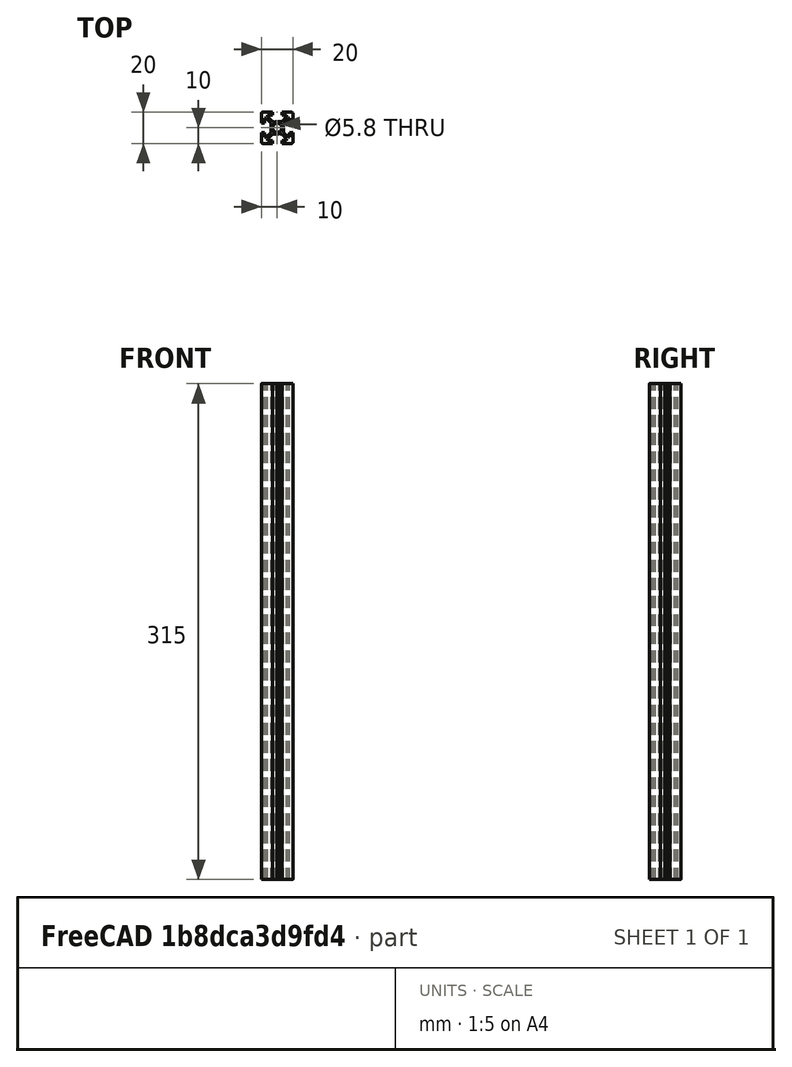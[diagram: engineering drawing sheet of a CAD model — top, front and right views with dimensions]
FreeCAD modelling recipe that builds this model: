
FCSTD DOCUMENT  (FreeCAD 0.17R13519 (Git))
Label: Z_Profile_2020_bed_side
License: All rights reserved
LicenseURL: http://en.wikipedia.org/wiki/All_rights_reserved
objects: Sketcher::SketchObject×1, PartDesign::Pad×1, PartDesign::Body×1
note: 4 computed .brp shape members not serialized (recipe doc carries the construction recipe); baked Part::Feature solids carry a one-line shape summary decoded from their .brp

FEATURE [Sketcher::SketchObject] Sketch001
  MapMode = 4
  sketch-geometry (77):
    g0: LineSegment StartX=-8 StartY=-3 StartZ=0 EndX=-10 EndY=-3 EndZ=0
    g1: LineSegment StartX=-10 StartY=-3 StartZ=0 EndX=-10 EndY=-9 EndZ=0
    g2: ArcOfCircle CenterX=-9 CenterY=-9 CenterZ=0 NormalX=0 NormalY=0 NormalZ=1 AngleXU=0 Radius=1 StartAngle=3.14159 EndAngle=4.71239
    g3: LineSegment StartX=-9 StartY=-10 StartZ=0 EndX=-3 EndY=-10 EndZ=0
    g4: LineSegment StartX=-3 StartY=-10 StartZ=0 EndX=-3 EndY=-8 EndZ=0
    g5: LineSegment StartX=-3 StartY=-8 StartZ=0 EndX=-6 EndY=-8 EndZ=0
    g6: LineSegment StartX=-6 StartY=-8 StartZ=0 EndX=-6 EndY=-7.06066 EndZ=0
    g7: LineSegment StartX=-6 StartY=-7.06066 StartZ=0 EndX=-2.93934 EndY=-4 EndZ=0
    g8: LineSegment StartX=-2.93934 StartY=-4 StartZ=0 EndX=-0.65359 EndY=-4 EndZ=0
    g9: ArcOfCircle CenterX=-0.65359 CenterY=-3.5 CenterZ=0 NormalX=0 NormalY=0 NormalZ=1 AngleXU=0 Radius=0.5 StartAngle=4.71239 EndAngle=5.23599
    g10: LineSegment StartX=-0.40359 StartY=-3.93301 StartZ=0 EndX=0 EndY=-3.7 EndZ=0
    g11: LineSegment StartX=0 StartY=-3.7 StartZ=0 EndX=0.40359 EndY=-3.93301 EndZ=0
    g12: ArcOfCircle CenterX=0.65359 CenterY=-3.5 CenterZ=0 NormalX=0 NormalY=0 NormalZ=1 AngleXU=0 Radius=0.5 StartAngle=4.18879 EndAngle=5.23599
    g13: LineSegment StartX=0.90359 StartY=-3.93301 StartZ=0 EndX=1.21889 EndY=-3.75098 EndZ=0
    g14: LineSegment StartX=1.21889 StartY=-3.75098 StartZ=0 EndX=2.5 EndY=-4 EndZ=0
    g15: LineSegment StartX=2.5 StartY=-4 StartZ=0 EndX=2.93934 EndY=-4 EndZ=0
    g16: LineSegment StartX=2.93934 StartY=-4 StartZ=0 EndX=6 EndY=-7.06066 EndZ=0
    g17: LineSegment StartX=6 StartY=-7.06066 StartZ=0 EndX=6 EndY=-8 EndZ=0
    g18: LineSegment StartX=6 StartY=-8 StartZ=0 EndX=3 EndY=-8 EndZ=0
    g19: LineSegment StartX=3 StartY=-8 StartZ=0 EndX=3 EndY=-10 EndZ=0
    g20: LineSegment StartX=3 StartY=-10 StartZ=0 EndX=9 EndY=-10 EndZ=0
    g21: ArcOfCircle CenterX=9 CenterY=-9 CenterZ=0 NormalX=0 NormalY=0 NormalZ=1 AngleXU=0 Radius=1 StartAngle=4.71239 EndAngle=6.28319
    g22: LineSegment StartX=10 StartY=-9 StartZ=0 EndX=10 EndY=-3 EndZ=0
    g23: LineSegment StartX=10 StartY=-3 StartZ=0 EndX=8 EndY=-3 EndZ=0
    g24: LineSegment StartX=8 StartY=-3 StartZ=0 EndX=8 EndY=-6 EndZ=0
    g25: LineSegment StartX=8 StartY=-6 StartZ=0 EndX=7.06066 EndY=-6 EndZ=0
    g26: LineSegment StartX=7.06066 StartY=-6 StartZ=0 EndX=4 EndY=-2.93934 EndZ=0
    g27: LineSegment StartX=4 StartY=-2.93934 StartZ=0 EndX=4 EndY=-0.65359 EndZ=0
    g28: ArcOfCircle CenterX=3.5 CenterY=-0.65359 CenterZ=0 NormalX=0 NormalY=0 NormalZ=1 AngleXU=0 Radius=0.5 StartAngle=0 EndAngle=0.523599
    g29: LineSegment StartX=3.93301 StartY=-0.40359 StartZ=0 EndX=3.7 EndY=0 EndZ=0
    g30: LineSegment StartX=3.7 StartY=0 StartZ=0 EndX=3.93301 EndY=0.40359 EndZ=0
    g31: ArcOfCircle CenterX=3.5 CenterY=0.65359 CenterZ=0 NormalX=0 NormalY=0 NormalZ=1 AngleXU=0 Radius=0.5 StartAngle=5.75959 EndAngle=6.80678
    g32: LineSegment StartX=3.93301 StartY=0.90359 StartZ=0 EndX=3.75098 EndY=1.21889 EndZ=0
    g33: LineSegment StartX=3.75098 StartY=1.21889 StartZ=0 EndX=4 EndY=2.5 EndZ=0
    g34: LineSegment StartX=4 StartY=2.5 StartZ=0 EndX=4 EndY=2.93934 EndZ=0
    g35: LineSegment StartX=4 StartY=2.93934 StartZ=0 EndX=7.06066 EndY=6 EndZ=0
    g36: LineSegment StartX=7.06066 StartY=6 StartZ=0 EndX=8 EndY=6 EndZ=0
    g37: LineSegment StartX=8 StartY=6 StartZ=0 EndX=8 EndY=3 EndZ=0
    g38: LineSegment StartX=8 StartY=3 StartZ=0 EndX=10 EndY=3 EndZ=0
    g39: LineSegment StartX=10 StartY=3 StartZ=0 EndX=10 EndY=9 EndZ=0
    g40: ArcOfCircle CenterX=9 CenterY=9 CenterZ=0 NormalX=0 NormalY=0 NormalZ=1 AngleXU=0 Radius=1 StartAngle=0 EndAngle=1.5708
    g41: LineSegment StartX=9 StartY=10 StartZ=0 EndX=3 EndY=10 EndZ=0
    g42: LineSegment StartX=3 StartY=10 StartZ=0 EndX=3 EndY=8 EndZ=0
    g43: LineSegment StartX=3 StartY=8 StartZ=0 EndX=6 EndY=8 EndZ=0
    g44: LineSegment StartX=6 StartY=8 StartZ=0 EndX=6 EndY=7.06066 EndZ=0
    g45: LineSegment StartX=6 StartY=7.06066 StartZ=0 EndX=2.93934 EndY=4 EndZ=0
    g46: LineSegment StartX=2.93934 StartY=4 StartZ=0 EndX=0.65359 EndY=4 EndZ=0
    g47: ArcOfCircle CenterX=0.65359 CenterY=3.5 CenterZ=0 NormalX=0 NormalY=0 NormalZ=1 AngleXU=0 Radius=0.5 StartAngle=1.5708 EndAngle=2.0944
    g48: LineSegment StartX=0.40359 StartY=3.93301 StartZ=0 EndX=0 EndY=3.7 EndZ=0
    g49: LineSegment StartX=0 StartY=3.7 StartZ=0 EndX=-0.40359 EndY=3.93301 EndZ=0
    g50: ArcOfCircle CenterX=-0.65359 CenterY=3.5 CenterZ=0 NormalX=0 NormalY=0 NormalZ=1 AngleXU=0 Radius=0.5 StartAngle=1.0472 EndAngle=2.0944
    g51: LineSegment StartX=-0.90359 StartY=3.93301 StartZ=0 EndX=-1.21889 EndY=3.75098 EndZ=0
    g52: LineSegment StartX=-1.21889 StartY=3.75098 StartZ=0 EndX=-2.5 EndY=4 EndZ=0
    g53: LineSegment StartX=-2.5 StartY=4 StartZ=0 EndX=-2.93934 EndY=4 EndZ=0
    g54: LineSegment StartX=-2.93934 StartY=4 StartZ=0 EndX=-6 EndY=7.06066 EndZ=0
    g55: LineSegment StartX=-6 StartY=7.06066 StartZ=0 EndX=-6 EndY=8 EndZ=0
    g56: LineSegment StartX=-6 StartY=8 StartZ=0 EndX=-3 EndY=8 EndZ=0
    g57: LineSegment StartX=-3 StartY=8 StartZ=0 EndX=-3 EndY=10 EndZ=0
    g58: LineSegment StartX=-3 StartY=10 StartZ=0 EndX=-9 EndY=10 EndZ=0
    g59: ArcOfCircle CenterX=-9 CenterY=9 CenterZ=0 NormalX=0 NormalY=0 NormalZ=1 AngleXU=0 Radius=1 StartAngle=1.5708 EndAngle=3.14159
    g60: LineSegment StartX=-10 StartY=9 StartZ=0 EndX=-10 EndY=3 EndZ=0
    g61: LineSegment StartX=-10 StartY=3 StartZ=0 EndX=-8 EndY=3 EndZ=0
    g62: LineSegment StartX=-8 StartY=3 StartZ=0 EndX=-8 EndY=6 EndZ=0
    g63: LineSegment StartX=-8 StartY=6 StartZ=0 EndX=-7.06066 EndY=6 EndZ=0
    g64: LineSegment StartX=-7.06066 StartY=6 StartZ=0 EndX=-4 EndY=2.93934 EndZ=0
    g65: LineSegment StartX=-4 StartY=2.93934 StartZ=0 EndX=-4 EndY=0.65359 EndZ=0
    g66: ArcOfCircle CenterX=-3.5 CenterY=0.65359 CenterZ=0 NormalX=0 NormalY=0 NormalZ=1 AngleXU=0 Radius=0.5 StartAngle=3.14159 EndAngle=3.66519
    g67: LineSegment StartX=-3.93301 StartY=0.40359 StartZ=0 EndX=-3.7 EndY=0 EndZ=0
    g68: LineSegment StartX=-3.7 StartY=0 StartZ=0 EndX=-3.93301 EndY=-0.40359 EndZ=0
    g69: ArcOfCircle CenterX=-3.5 CenterY=-0.65359 CenterZ=0 NormalX=0 NormalY=0 NormalZ=1 AngleXU=0 Radius=0.5 StartAngle=2.61799 EndAngle=3.66519
    g70: LineSegment StartX=-3.93301 StartY=-0.90359 StartZ=0 EndX=-3.75098 EndY=-1.21889 EndZ=0
    g71: LineSegment StartX=-3.75098 StartY=-1.21889 StartZ=0 EndX=-4 EndY=-2.5 EndZ=0
    g72: LineSegment StartX=-4 StartY=-2.5 StartZ=0 EndX=-4 EndY=-2.93934 EndZ=0
    g73: LineSegment StartX=-4 StartY=-2.93934 StartZ=0 EndX=-7.06066 EndY=-6 EndZ=0
    g74: LineSegment StartX=-7.06066 StartY=-6 StartZ=0 EndX=-8 EndY=-6 EndZ=0
    g75: LineSegment StartX=-8 StartY=-6 StartZ=0 EndX=-8 EndY=-3 EndZ=0
    g76: Circle CenterX=0 CenterY=0 CenterZ=0 NormalX=0 NormalY=0 NormalZ=1 AngleXU=0 Radius=2.9
  constraints (105):
    c: Horizontal(g0)
    c: Coincident(g0,g1)
    c: Vertical(g1)
    c: Coincident(g1,g2)
    c: Coincident(g2,g3)
    c: Horizontal(g3)
    c: Coincident(g3,g4)
    c: Coincident(g4,g5)
    c: Horizontal(g5)
    c: Coincident(g5,g6)
    c: Coincident(g6,g7)
    c: Coincident(g7,g8)
    c: Horizontal(g8)
    c: Coincident(g8,g9)
    c: Coincident(g9,g10)
    c: Coincident(g10,g11)
    c: Coincident(g11,g12)
    c: Coincident(g12,g13)
    c: Coincident(g13,g14)
    c: Coincident(g14,g15)
    c: Horizontal(g15)
    c: Coincident(g15,g16)
    c: Coincident(g16,g17)
    c: Coincident(g17,g18)
    c: Coincident(g18,g19)
    c: Vertical(g19)
    c: Coincident(g19,g20)
    c: Horizontal(g20)
    c: Coincident(g20,g21)
    c: Coincident(g21,g22)
    c: Vertical(g22)
    c: Coincident(g22,g23)
    c: Horizontal(g23)
    c: Coincident(g23,g24)
    c: Vertical(g24)
    c: Coincident(g24,g25)
    c: Coincident(g25,g26)
    c: Coincident(g26,g27)
    c: Vertical(g27)
    c: Coincident(g27,g28)
    c: Coincident(g28,g29)
    c: Coincident(g29,g30)
    c: Coincident(g30,g31)
    c: Coincident(g31,g32)
    c: Coincident(g32,g33)
    c: Coincident(g33,g34)
    c: Vertical(g34)
    c: Coincident(g34,g35)
    c: Coincident(g35,g36)
    c: Coincident(g36,g37)
    c: Coincident(g37,g38)
    c: Horizontal(g38)
    c: Coincident(g38,g39)
    c: Vertical(g39)
    c: Coincident(g39,g40)
    c: Coincident(g40,g41)
    c: Horizontal(g41)
    c: Coincident(g41,g42)
    c: Coincident(g42,g43)
    c: Horizontal(g43)
    c: Coincident(g43,g44)
    c: Coincident(g44,g45)
    c: Coincident(g45,g46)
    c: Horizontal(g46)
    c: Coincident(g46,g47)
    c: Coincident(g47,g48)
    c: Coincident(g48,g49)
    c: Coincident(g49,g50)
    c: Coincident(g50,g51)
    c: Coincident(g51,g52)
    c: Coincident(g52,g53)
    c: Horizontal(g53)
    c: Coincident(g53,g54)
    c: Coincident(g54,g55)
    c: Vertical(g55)
    c: Coincident(g55,g56)
    c: Coincident(g56,g57)
    c: Vertical(g57)
    c: Coincident(g57,g58)
    c: Horizontal(g58)
    c: Coincident(g58,g59)
    c: Coincident(g59,g60)
    c: Vertical(g60)
    c: Coincident(g60,g61)
    c: Horizontal(g61)
    c: Coincident(g61,g62)
    c: Vertical(g62)
    c: Coincident(g62,g63)
    c: Horizontal(g63)
    c: Coincident(g63,g64)
    c: Coincident(g64,g65)
    c: Vertical(g65)
    c: Coincident(g65,g66)
    c: Coincident(g66,g67)
    c: Coincident(g67,g68)
    c: Coincident(g68,g69)
    c: Coincident(g69,g70)
    c: Coincident(g70,g71)
    c: Coincident(g71,g72)
    c: Vertical(g72)
    c: Coincident(g72,g73)
    c: Coincident(g73,g74)
    c: Coincident(g74,g75)
    c: Coincident(g75,g0)
    c: Radius(g76) = 2.9
FEATURE [PartDesign::Pad] Pad
  Length = 315
  Length2 = 100
  Midplane = true
  Profile = -> Sketch001
  Type = 0
FEATURE [PartDesign::Body] Body
  Group = -> [Sketch001,Pad]
  Origin = -> Origin
  Tip = -> Pad
